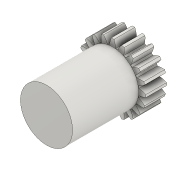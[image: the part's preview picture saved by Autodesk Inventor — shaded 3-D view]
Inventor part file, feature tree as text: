
AUTODESK INVENTOR PART (.ipt)
format: ipt  version: 2020.3 (Build 243373010, 373A)  size: 221,184 bytes
history: native  units: mm (DEFAULTED — no unit token found)
features: plane x3, other x3, sketch x3, extrude x2
ambient origin geometry x8: Origin, YZ Plane, XZ Plane, XY Plane, X Axis, Y Axis, Z Axis, Center Point
bodies: Solid1 (feature_tree)
feature tree (11):
  extrude  "Extrusion1"  Depth=10.0mm TaperAngle=0.0deg
  plane  "Work Plane2"
  plane  "Work Plane8"
  plane  "Work Plane9"
  other  "Spur Gear"
  extrude  "Extrusion2"  Depth=10.0mm TaperAngle=0.0deg
  sketch  "Sketch1"  dims[d0=31.9mm d1=10.0mm d2=0.0mm]
  sketch  "Sketch2"  dims[d3=29.0mm d4=10.0mm d5=0.0mm]
  other  "Srf1"
  sketch  "Sketch3"  dims[d16=32.625mm d17=0.0mm d34=1.570796mm d39=0.0mm d41=0.0mm d43=32.625mm d46=32.625mm d47=0.0mm d48=0.0mm d49=25.0mm d50=31.77mm d51=0.0mm]
  other  "Pitch Diameter"
